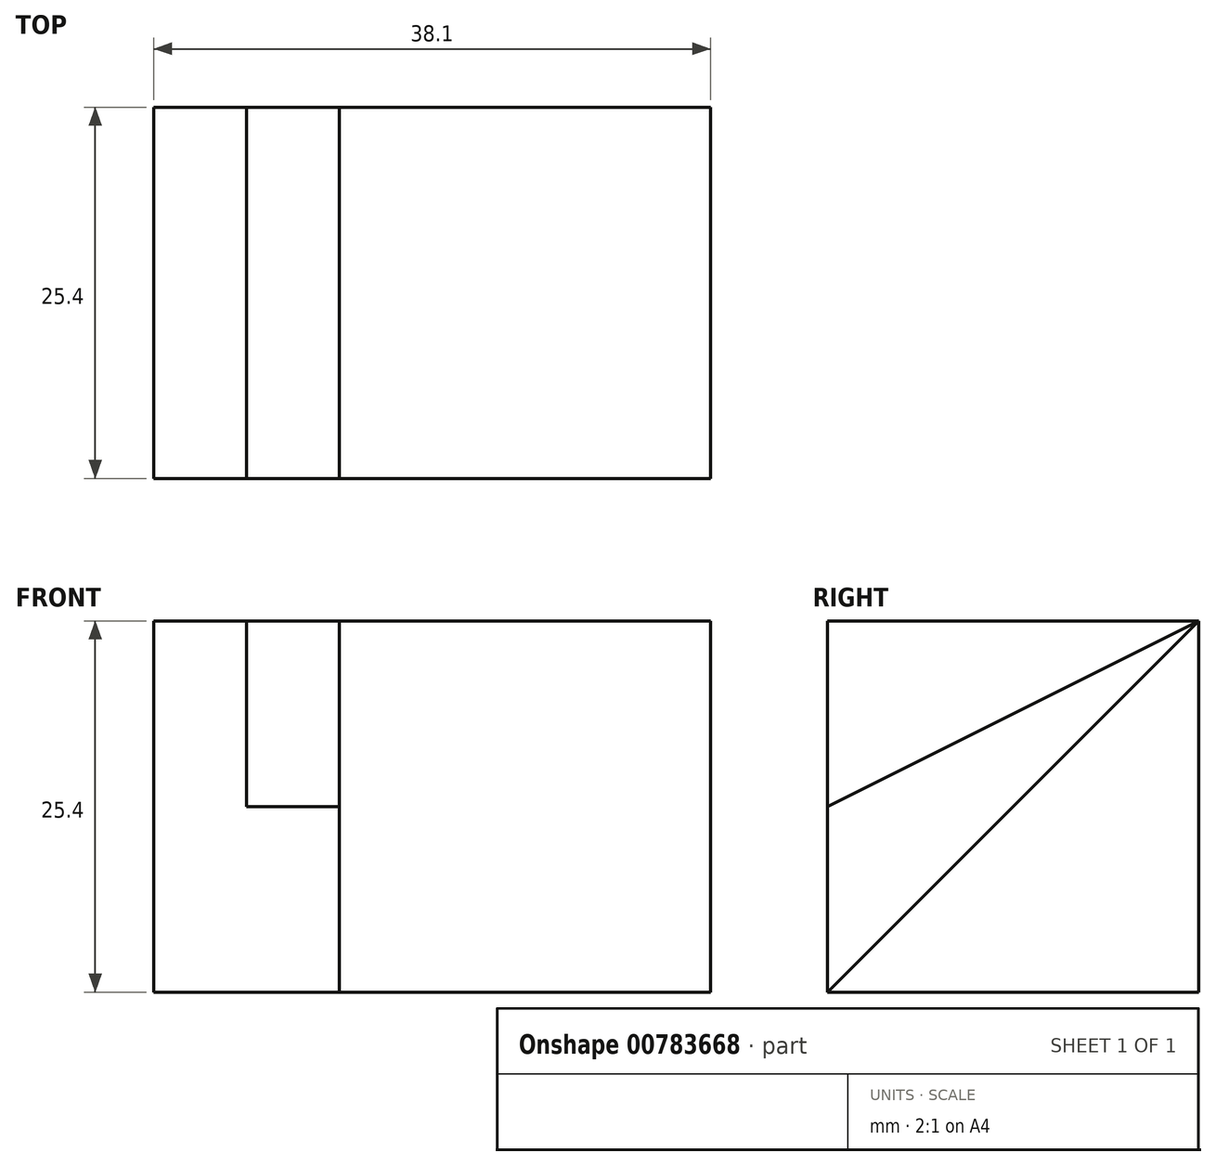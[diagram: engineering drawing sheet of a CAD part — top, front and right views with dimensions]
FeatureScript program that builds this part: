
annotation { "Feature Type Name" : "Feature", "Feature Type Description" : "" }
export const myFeature = defineFeature(function(context is Context, id is Id, definition is map)
    precondition{}
    {
        {
            var Q0;
            Q0=qCreatedBy(makeId("Front.planeOp"),FACE);
            var sketch = newSketch(context, id + "F0", { "sketchPlane" : qUnion([Q0])});
            skLineSegment(sketch, "E0", {"start": v(0, 0) * mm, "end": v(38.1, 0) * mm});
            skLineSegment(sketch, "E1", {"start": v(38.1, 0) * mm, "end": v(38.1, 25.4) * mm});
            skLineSegment(sketch, "E2", {"start": v(38.1, 25.4) * mm, "end": v(0, 25.4) * mm});
            skLineSegment(sketch, "E3", {"start": v(0, 25.4) * mm, "end": v(0, 0) * mm});
            skSolve(sketch);
        }
        {
            var Q0;
            Q0 = qSketchRegion(id + "F0", true);
            extrude(context, id + "F1", {"entities" : qUnion([Q0]), "depth" : 25.4 * mm, "offsetDistance" : 25.4 * mm});
        }
        {
            var Q0;
            Q0=makeQuery(id+"F1.opExtrude","SWEPT_FACE",FACE,{"disambiguationData":[OSD([sQuery(id+"F0.wireOp",EDGE,"E1")])]});
            var sketch = newSketch(context, id + "F2", { "sketchPlane" : qUnion([Q0])});
            skLineSegment(sketch, "E4", {"start": v(0, 25.4) * mm, "end": v(-25.4, 0) * mm});
            skSolve(sketch);
        }
        {
            var Q0;
            Q0=makeQuery(id+"F2.imprint","IMPRINT",FACE,{"disambiguationData":[TD([[makeQuery(id+"F2.imprint","IMPRINT",EDGE,{"derivedFrom":sQuery(id+"F2.wireOp",EDGE,"E4")}),-1.0]])]});
            extrude(context, id + "F3", {"entities" : qUnion([Q0]), "operationType" : NewBodyOperationType.REMOVE, "oppositeDirection" : true, "depth" : 25.4 * mm, "offsetDistance" : 25.4 * mm});
        }
        {
            var Q0;
            Q0=makeQuery(id+"F3.boolean.opBoolean","COPY",FACE,{"derivedFrom":makeQuery(id+"F3.opExtrude","CAP_FACE",FACE,{"disambiguationData":[OSD([sQuery(id+"F0.wireOp",EDGE,"E1"),sQuery(id+"F0.wireOp",EDGE,"E2"),sQuery(id+"F2.wireOp",EDGE,"E4")])],"isStart":false})});
            var sketch = newSketch(context, id + "F4", { "sketchPlane" : qUnion([Q0])});
            skLineSegment(sketch, "E5", {"start": v(-25.4, 0) * mm, "end": v(-25.4, 12.7) * mm});
            skLineSegment(sketch, "E6", {"start": v(0, 25.4) * mm, "end": v(-25.4, 12.7) * mm});
            skSolve(sketch);
        }
        {
            var Q0;
            {var subQ0=sQuery(id+"F4.wireOp",EDGE,"E6");Q0=makeQuery(id+"F4.imprint","IMPRINT",FACE,{"disambiguationData":[TD([[makeQuery(id+"F4.imprint","IMPRINT",EDGE,{"derivedFrom":subQ0}),-1.0]])]});}
            extrude(context, id + "F5", {"entities" : qUnion([Q0]), "operationType" : NewBodyOperationType.REMOVE, "oppositeDirection" : true, "depth" : 6.35 * mm, "offsetDistance" : 25.4 * mm});
        }
    });
